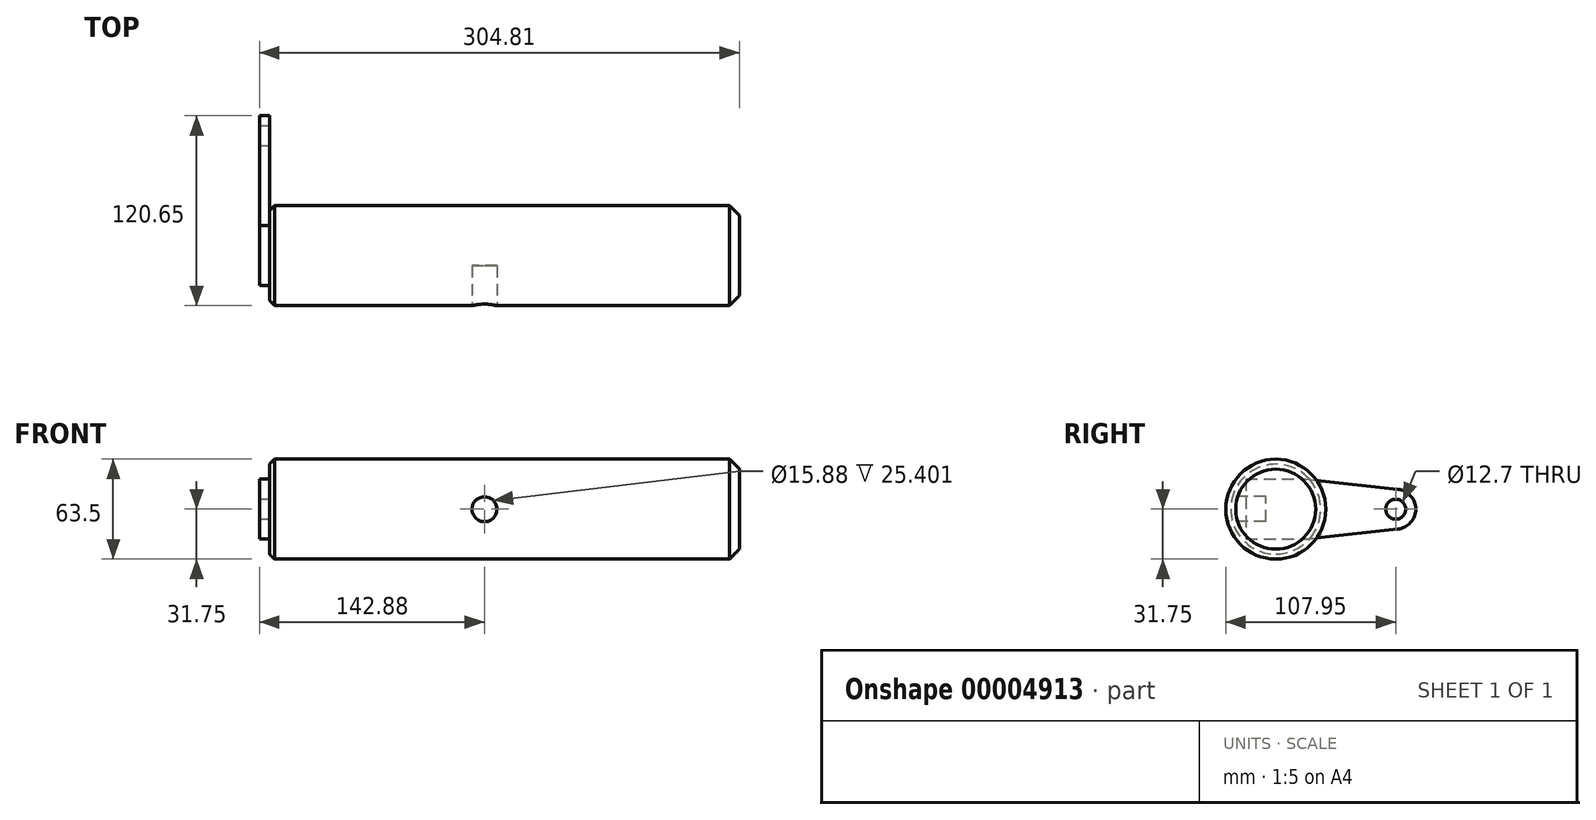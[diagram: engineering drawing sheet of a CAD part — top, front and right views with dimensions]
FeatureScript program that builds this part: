
annotation { "Feature Type Name" : "Feature", "Feature Type Description" : "" }
export const myFeature = defineFeature(function(context is Context, id is Id, definition is map)
    precondition{}
    {
        {
            var Q0;
            Q0=qCreatedBy(makeId("Right.planeOp"),FACE);
            var sketch = newSketch(context, id + "F0", { "sketchPlane" : qUnion([Q0])});
            skCircle(sketch, "E0", {"center": v(0, 0) * mm, "radius": 31.75 * mm});
            skSolve(sketch);
        }
        {
            var Q0;
            Q0=makeQuery(id+"F0.imprint","IMPRINT",FACE,{"disambiguationData":[TD([[makeQuery(id+"F0.imprint","IMPRINT",EDGE,{"derivedFrom":sQuery(id+"F0.wireOp",EDGE,"E0")}),1.0]])]});
            extrude(context, id + "F1", {"entities" : qUnion([Q0]), "endBound" : BoundingType.SYMMETRIC, "depth" : 298.45 * mm});
        }
        {
            var Q0;
            Q0=makeQuery(id+"F1.opExtrude","CAP_EDGE",EDGE,{"disambiguationData":[OSD([sQuery(id+"F0.wireOp",EDGE,"E0")])],"isStart":false});
            chamfer(context, id + "F2", {"entities" : qUnion([Q0]), "width" : 6.35 * mm, "tangentPropagation" : true});
        }
        {
            var Q0;
            Q0=makeQuery(id+"F1.opExtrude","CAP_EDGE",EDGE,{"disambiguationData":[OSD([sQuery(id+"F0.wireOp",EDGE,"E0")])],"isStart":true});
            chamfer(context, id + "F3", {"entities" : qUnion([Q0]), "width" : 3.17 * mm, "tangentPropagation" : true});
        }
        {
            var Q0;
            Q0=qCreatedBy(makeId("Front.planeOp"),FACE);
            cPlane(context, id + "F4", {"entities" : qUnion([Q0]), "cplaneType" : CPlaneType.OFFSET, "offset" : 31.75 * mm, "width" : 152.4 * mm, "height" : 152.4 * mm});
        }
        {
            var Q0;
            Q0=qCreatedBy(id+"F4.planeOp",FACE);
            var sketch = newSketch(context, id + "F5", { "sketchPlane" : qUnion([Q0])});
            skLineSegment(sketch, "E1.0", {"start": v(-12.7, 28.57) * mm, "end": v(-12.7, -28.57) * mm, "construction": true});
            skCircle(sketch, "E2", {"center": v(-12.7, 0) * mm, "radius": 7.94 * mm});
            skSolve(sketch);
        }
        {
            var Q0;
            Q0 = qSketchRegion(id + "F5", true);
            extrude(context, id + "F6", {"entities" : qUnion([Q0]), "operationType" : NewBodyOperationType.REMOVE, "oppositeDirection" : true, "depth" : 25.4 * mm});
        }
        {
            var Q0;
            Q0=makeQuery(id+"F1.opExtrude","CAP_FACE",FACE,{"disambiguationData":[OSD([sQuery(id+"F0.wireOp",EDGE,"E0")])],"isStart":true});
            var sketch = newSketch(context, id + "F7", { "sketchPlane" : qUnion([Q0])});
            skLineSegment(sketch, "E3", {"start": v(0, 0) * mm, "end": v(0, 19.05) * mm, "construction": true});
            skLineSegment(sketch, "E4", {"start": v(0, 0) * mm, "end": v(-76.2, 0) * mm, "construction": true});
            skLineSegment(sketch, "E5.0", {"start": v(19.05, 0) * mm, "end": v(19.05, 19.05) * mm});
            skArc(sketch, "E6", {"start": v(-77.59, 12.62) * mm, "mid": v(-88.9, 0) * mm, "end": v(-77.59, -12.62) * mm});
            skCircle(sketch, "E7", {"center": v(-76.2, 0) * mm, "radius": 6.35 * mm});
            skLineSegment(sketch, "E8", {"start": v(19.05, 19.05) * mm, "end": v(-19.05, 19.05) * mm});
            skLineSegment(sketch, "E9", {"start": v(-19.05, 19.05) * mm, "end": v(-77.59, 12.62) * mm});
            skLineSegment(sketch, "E10.0.MirrorCS", {"start": v(-19.05, -19.05) * mm, "end": v(-77.59, -12.62) * mm});
            skLineSegment(sketch, "E11.0.MirrorCS", {"start": v(19.05, -19.05) * mm, "end": v(-19.05, -19.05) * mm});
            skLineSegment(sketch, "E12.0.MirrorCS", {"start": v(19.05, 0) * mm, "end": v(19.05, -19.05) * mm});
            skSolve(sketch);
        }
        {
            var Q0;
            {var subQ9=sQuery(id+"F7.wireOp",EDGE,"E6");Q0=qUnion([makeQuery(id+"F7.imprint","IMPRINT",FACE,{"disambiguationData":[TD([[makeQuery(id+"F7.imprint","IMPRINT",EDGE,{"derivedFrom":sQuery(id+"F7.wireOp",EDGE,"E5.0")}),1.0]])]}),makeQuery(id+"F7.imprint","IMPRINT",FACE,{"disambiguationData":[TD([[makeQuery(id+"F7.imprint","IMPRINT",EDGE,{"derivedFrom":subQ9}),1.0]])]})]);}
            extrude(context, id + "F8", {"entities" : qUnion([Q0]), "operationType" : NewBodyOperationType.ADD, "depth" : 6.35 * mm});
        }
    });
